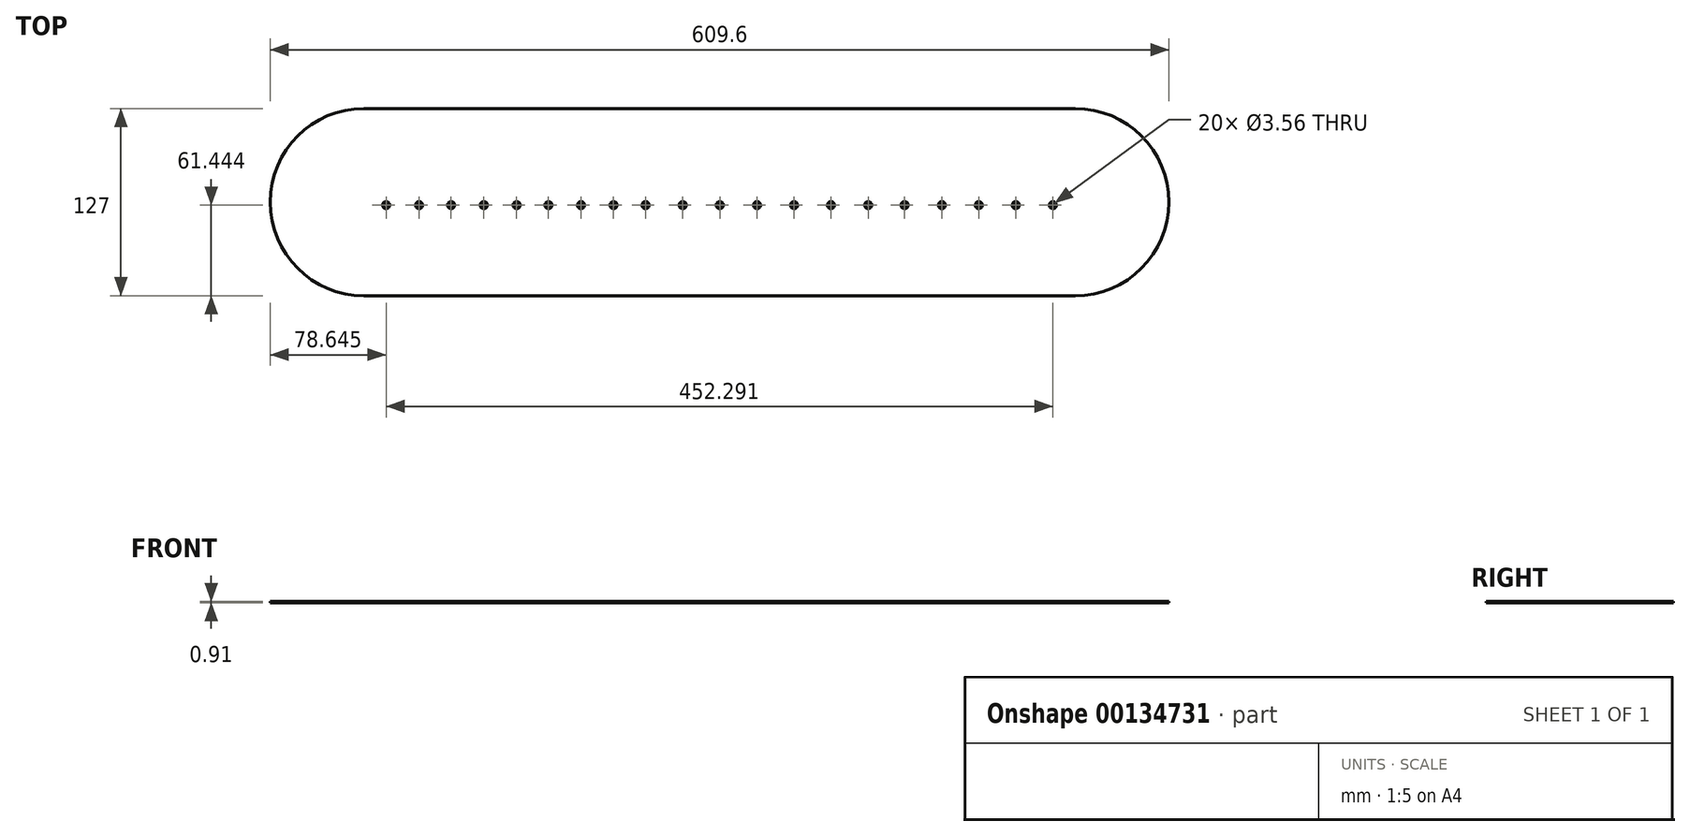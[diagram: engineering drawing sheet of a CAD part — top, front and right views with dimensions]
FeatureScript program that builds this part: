
annotation { "Feature Type Name" : "Feature", "Feature Type Description" : "" }
export const myFeature = defineFeature(function(context is Context, id is Id, definition is map)
    precondition{}
    {
        {
            var Q0;
            Q0=qCreatedBy(makeId("Top.planeOp"),FACE);
            var sketch = newSketch(context, id + "F0", { "sketchPlane" : qUnion([Q0])});
            skLineSegment(sketch, "E0", {"start": v(-241.3, 0) * mm, "end": v(241.3, 0) * mm, "construction": true});
            skArc(sketch, "E1.0.startCap", {"start": v(-241.3, -63.5) * mm, "mid": v(-304.8, 0) * mm, "end": v(-241.3, 63.5) * mm});
            skArc(sketch, "E1.0.endCap", {"start": v(241.3, 63.5) * mm, "mid": v(304.8, 0) * mm, "end": v(241.3, -63.5) * mm});
            skLineSegment(sketch, "E1.0.left", {"start": v(-241.3, 63.5) * mm, "end": v(241.3, 63.5) * mm});
            skLineSegment(sketch, "E1.0.right", {"start": v(-241.3, -63.5) * mm, "end": v(241.3, -63.5) * mm});
            skSolve(sketch);
        }
        {
            var Q0;
            Q0 = qSketchRegion(id + "F0", true);
            extrude(context, id + "F1", {"entities" : qUnion([Q0]), "depth" : 0.91 * mm});
        }
        {
            var Q0;
            Q0=makeQuery(id+"F1.opExtrude","CAP_FACE",FACE,{"disambiguationData":[OSD([sQuery(id+"F0.wireOp",EDGE,"E1.0.startCap"),sQuery(id+"F0.wireOp",EDGE,"E1.0.endCap"),sQuery(id+"F0.wireOp",EDGE,"E1.0.left"),sQuery(id+"F0.wireOp",EDGE,"E1.0.right")])],"isStart":false});
            var sketch = newSketch(context, id + "F2", { "sketchPlane" : qUnion([Q0])});
            skPoint(sketch, "E2", {"position": v(0.18, -2.06) * mm});
            skPoint(sketch, "E3", {"position": v(25.45, -2.06) * mm});
            skPoint(sketch, "E4", {"position": v(50.55, -2.06) * mm});
            skPoint(sketch, "E5", {"position": v(75.57, -2.06) * mm});
            skPoint(sketch, "E6", {"position": v(100.86, -2.06) * mm});
            skPoint(sketch, "E7", {"position": v(125.53, -2.06) * mm});
            skPoint(sketch, "E8", {"position": v(150.83, -2.06) * mm});
            skPoint(sketch, "E9", {"position": v(175.87, -2.06) * mm});
            skPoint(sketch, "E10", {"position": v(200.94, -2.06) * mm});
            skPoint(sketch, "E11", {"position": v(226.14, -2.06) * mm});
            skPoint(sketch, "E12", {"position": v(-24.96, -2.06) * mm});
            skPoint(sketch, "E13", {"position": v(-50.18, -2.06) * mm});
            skPoint(sketch, "E14", {"position": v(-159.91, -2.06) * mm});
            skPoint(sketch, "E15", {"position": v(-71.93, -2.06) * mm});
            skPoint(sketch, "E16", {"position": v(-226.16, -2.06) * mm});
            skPoint(sketch, "E17", {"position": v(-94, -2.06) * mm});
            skPoint(sketch, "E18", {"position": v(-203.8, -2.06) * mm});
            skPoint(sketch, "E19", {"position": v(-116.05, -2.06) * mm});
            skPoint(sketch, "E20", {"position": v(-182.09, -2.06) * mm});
            skPoint(sketch, "E21", {"position": v(-137.66, -2.06) * mm});
            skPoint(sketch, "E22.0", {"position": v(-304.8, 0) * mm});
            skPoint(sketch, "E23.0", {"position": v(304.8, 0) * mm});
            skSolve(sketch);
        }
        {
            var Q0;
            Q0=sQuery(id+"F2.wireOp",VERTEX,"E16");
            var Q1;
            Q1=sQuery(id+"F2.wireOp",VERTEX,"E18");
            var Q2;
            Q2=sQuery(id+"F2.wireOp",VERTEX,"E20");
            var Q3;
            Q3=sQuery(id+"F2.wireOp",VERTEX,"E14");
            var Q4;
            Q4=sQuery(id+"F2.wireOp",VERTEX,"E21");
            var Q5;
            Q5=sQuery(id+"F2.wireOp",VERTEX,"E19");
            var Q6;
            Q6=sQuery(id+"F2.wireOp",VERTEX,"E17");
            var Q7;
            Q7=sQuery(id+"F2.wireOp",VERTEX,"E15");
            var Q8;
            Q8=sQuery(id+"F2.wireOp",VERTEX,"E13");
            var Q9;
            Q9=sQuery(id+"F2.wireOp",VERTEX,"E12");
            var Q10;
            Q10=sQuery(id+"F2.wireOp",VERTEX,"E2");
            var Q11;
            Q11=sQuery(id+"F2.wireOp",VERTEX,"E3");
            var Q12;
            Q12=sQuery(id+"F2.wireOp",VERTEX,"E4");
            var Q13;
            Q13=sQuery(id+"F2.wireOp",VERTEX,"E5");
            var Q14;
            Q14=sQuery(id+"F2.wireOp",VERTEX,"E6");
            var Q15;
            Q15=sQuery(id+"F2.wireOp",VERTEX,"E7");
            var Q16;
            Q16=sQuery(id+"F2.wireOp",VERTEX,"E8");
            var Q17;
            Q17=sQuery(id+"F2.wireOp",VERTEX,"E9");
            var Q18;
            Q18=sQuery(id+"F2.wireOp",VERTEX,"E10");
            var Q19;
            Q19=sQuery(id+"F2.wireOp",VERTEX,"E11");
            var Q20;
            Q20=makeQuery(id+"F1.opExtrude","SWEPT_BODY",BODY,{"disambiguationData":[OSD([sQuery(id+"F0.wireOp",EDGE,"E1.0.startCap"),sQuery(id+"F0.wireOp",EDGE,"E1.0.endCap"),sQuery(id+"F0.wireOp",EDGE,"E1.0.left"),sQuery(id+"F0.wireOp",EDGE,"E1.0.right")])]});
            hole(context, id + "F3", {"style" : HoleStyle.C_SINK, "endStyle" : HoleEndStyle.THROUGH, "holeDiameter" : 3.56 * mm, "cSinkDiameter" : 4.83 * mm, "cSinkAngle" : 100 * degree, "majorDiameter" : 6.35 * mm, "locations" : qUnion([Q0, Q1, Q2, Q3, Q4, Q5, Q6, Q7, Q8, Q9, Q10, Q11, Q12, Q13, Q14, Q15, Q16, Q17, Q18, Q19]), "scope" : qUnion([Q20]), "isTappedThrough" : true, "tappedDepth" : 12.7 * mm, "tapClearance" : 3});
        }
    });
